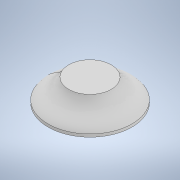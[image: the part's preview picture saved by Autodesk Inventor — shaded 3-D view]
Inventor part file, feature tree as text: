
AUTODESK INVENTOR PART (.ipt)
format: ipt  version: 2021 (Build 250183000, 183)  size: 146,432 bytes
history: native  units: mm
features: revolve x1, sketch x1
ambient origin geometry x8: Origin, YZ Plane, XZ Plane, XY Plane, X Axis, Y Axis, Z Axis, Center Point
bodies: Solid1 (feature_tree)
feature tree (2):
  revolve  "Revolution1"  [1 undecoded]
  sketch  "Sketch1"  dims[d0=75.0mm d1=40.0mm d2=38.0mm d3=5.0mm d4=90.0deg]
note: 1 required parameter value undecoded (feature->parameter linkage not recoverable at this tier; creation-order binding heuristic only, values carry confidence <= 0.55)
